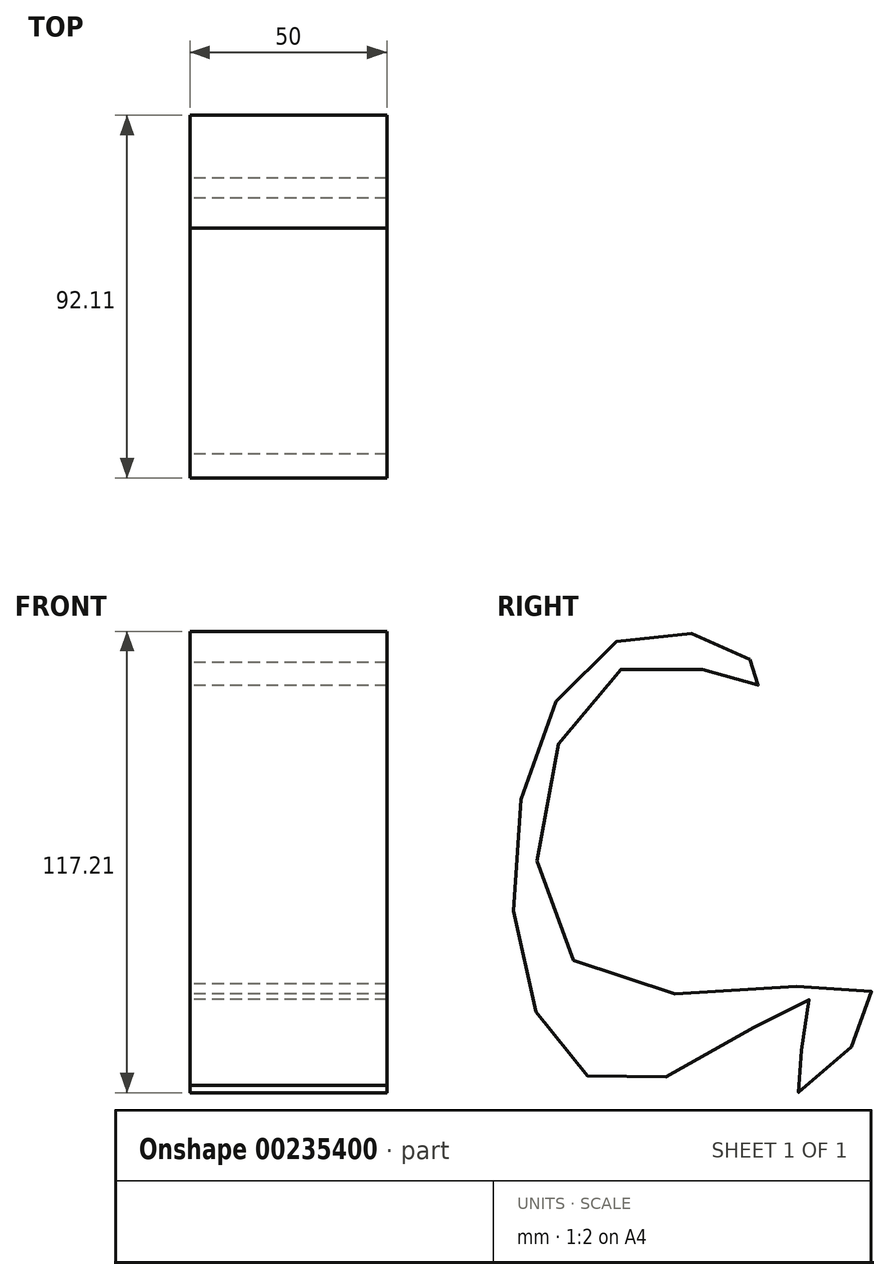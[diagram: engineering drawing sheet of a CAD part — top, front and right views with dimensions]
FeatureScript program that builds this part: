
annotation { "Feature Type Name" : "Feature", "Feature Type Description" : "" }
export const myFeature = defineFeature(function(context is Context, id is Id, definition is map)
    precondition{}
    {
        {
            var Q0;
            Q0=qCreatedBy(makeId("Right.planeOp"),FACE);
            var sketch = newSketch(context, id + "F0", { "sketchPlane" : qUnion([Q0])});
            skFitSpline(sketch, "E0", {"points": [v(0, 52.1) * mm, v(-36.13, 55.46) * mm, v(-59.42, -17.77) * mm, v(-28.21, -55.94) * mm, v(15.73, -35.05) * mm, v(11.4, -57.86) * mm, v(31.81, -33.85) * mm, v(-42.14, -26.65) * mm, v(-33.97, 48.98) * mm, v(2.52, 45.62) * mm, v(0, 52.1) * mm]});
            skSolve(sketch);
        }
        {
            var Q0;
            Q0=makeQuery(id+"F0.imprint","IMPRINT",FACE,{"disambiguationData":[TD([[makeQuery(id+"F0.imprint","IMPRINT",EDGE,{"derivedFrom":sQuery(id+"F0.wireOp",EDGE,"E0")}),1.0]])]});
            extrude(context, id + "F1", {"entities" : qUnion([Q0]), "endBound" : BoundingType.SYMMETRIC, "depth" : 50 * mm});
        }
    });
